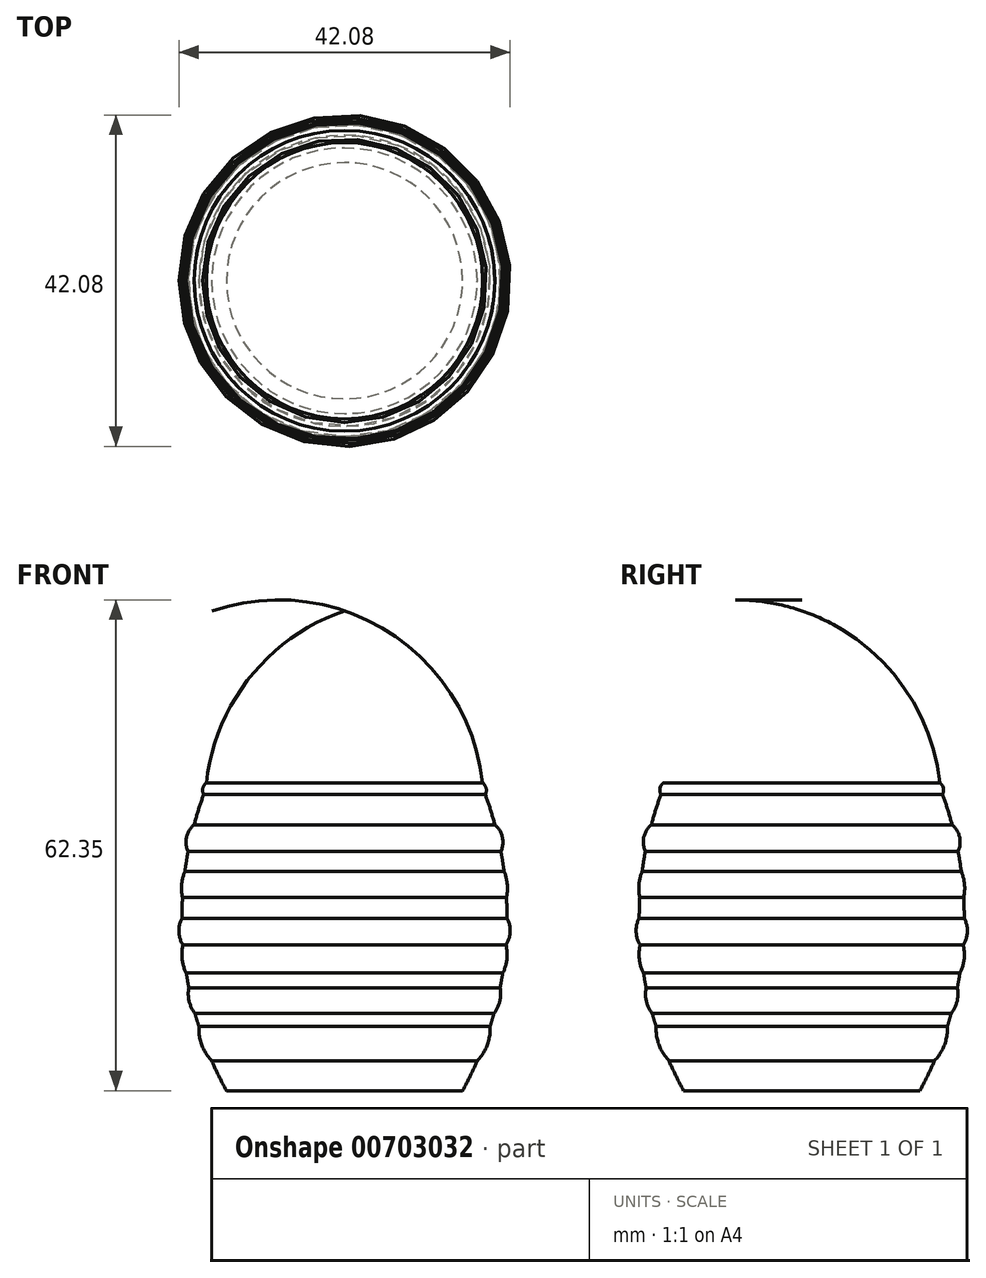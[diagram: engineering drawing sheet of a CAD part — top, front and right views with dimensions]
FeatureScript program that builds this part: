
annotation { "Feature Type Name" : "Feature", "Feature Type Description" : "" }
export const myFeature = defineFeature(function(context is Context, id is Id, definition is map)
    precondition{}
    {
        {
            var Q0;
            Q0=qCreatedBy(makeId("Front.planeOp"),FACE);
            var sketch = newSketch(context, id + "F0", { "sketchPlane" : qUnion([Q0])});
            skLineSegment(sketch, "E0", {"start": v(0, 0) * mm, "end": v(0, 60.96) * mm});
            skLineSegment(sketch, "E1", {"start": v(0, 0) * mm, "end": v(-15, 0) * mm});
            skArc(sketch, "E2", {"start": v(0, 60.96) * mm, "mid": v(-11.95, 52.59) * mm, "end": v(-17.54, 39.1) * mm});
            skArc(sketch, "E3", {"start": v(-17.89, 37.63) * mm, "mid": v(-18.54, 35.72) * mm, "end": v(-19.1, 33.79) * mm});
            skPoint(sketch, "E4.visualSharp", {"position": v(-17.61, 38.36) * mm});
            skArc(sketch, "E5", {"start": v(-18.5, 8.14) * mm, "mid": v(-18.13, 5.8) * mm, "end": v(-16.87, 3.81) * mm});
            skArc(sketch, "E6", {"start": v(-19.76, 13.06) * mm, "mid": v(-19.74, 11.36) * mm, "end": v(-19, 9.84) * mm});
            skArc(sketch, "E7", {"start": v(-20.51, 18.5) * mm, "mid": v(-20.63, 16.68) * mm, "end": v(-20.1, 14.94) * mm});
            skArc(sketch, "E8", {"start": v(-20.64, 21.9) * mm, "mid": v(-21.04, 20.19) * mm, "end": v(-20.51, 18.5) * mm});
            skArc(sketch, "E9", {"start": v(-20.27, 27.87) * mm, "mid": v(-20.68, 26.23) * mm, "end": v(-20.57, 24.53) * mm});
            skArc(sketch, "E10", {"start": v(-19.1, 33.79) * mm, "mid": v(-20.05, 32.22) * mm, "end": v(-19.87, 30.4) * mm});
            skArc(sketch, "E11", {"start": v(-17.54, 39.1) * mm, "mid": v(-18, 38.43) * mm, "end": v(-17.89, 37.63) * mm});
            skArc(sketch, "E12.trimOffspring", {"start": v(-16.87, 3.81) * mm, "mid": v(-15.98, 1.88) * mm, "end": v(-15, 0) * mm});
            skArc(sketch, "E13.trimOffspring", {"start": v(-19, 9.84) * mm, "mid": v(-18.75, 8.99) * mm, "end": v(-18.5, 8.14) * mm});
            skArc(sketch, "E14.trimOffspring", {"start": v(-20.1, 14.94) * mm, "mid": v(-19.94, 14) * mm, "end": v(-19.76, 13.06) * mm});
            skArc(sketch, "E15.trimOffspring", {"start": v(-20.57, 24.53) * mm, "mid": v(-20.63, 23.22) * mm, "end": v(-20.64, 21.9) * mm});
            skArc(sketch, "E16.trimOffspring", {"start": v(-19.87, 30.4) * mm, "mid": v(-20.08, 29.14) * mm, "end": v(-20.27, 27.87) * mm});
            skSolve(sketch);
        }
        {
            var Q0;
            Q0 = qSketchRegion(id + "F0", true);
            var Q1;
            Q1=sQuery(id+"F0.wireOp",EDGE,"E0");
            revolve(context, id + "F1", {"surfaceOperationType" : NewSurfaceOperationType.NEW, "entities" : qUnion([Q0]), "axis" : qUnion([Q1]), "revolveType" : RevolveType.FULL});
        }
    });
